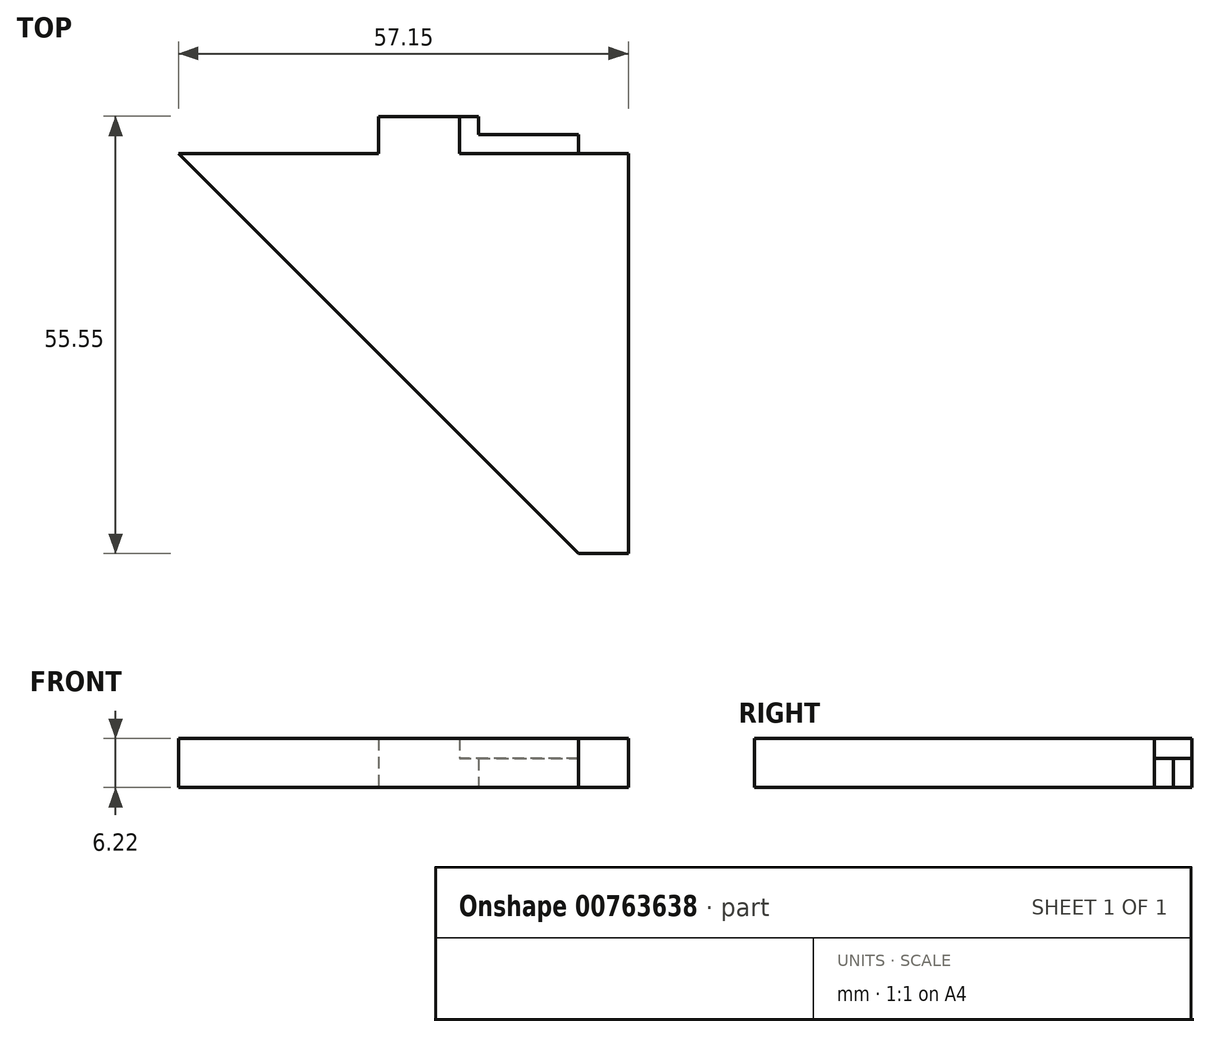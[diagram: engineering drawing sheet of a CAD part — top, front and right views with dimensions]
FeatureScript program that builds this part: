
annotation { "Feature Type Name" : "Feature", "Feature Type Description" : "" }
export const myFeature = defineFeature(function(context is Context, id is Id, definition is map)
    precondition{}
    {
        {
            var Q0;
            Q0=qCreatedBy(makeId("Top.planeOp"),FACE);
            var sketch = newSketch(context, id + "F0", { "sketchPlane" : qUnion([Q0])});
            skLineSegment(sketch, "E0.bottom", {"start": v(25.4, -25.4) * mm, "end": v(-25.4, -25.4) * mm});
            skLineSegment(sketch, "E0.top", {"start": v(25.4, 25.4) * mm, "end": v(-25.4, 25.4) * mm});
            skLineSegment(sketch, "E0.left", {"start": v(25.4, -25.4) * mm, "end": v(25.4, 25.4) * mm});
            skLineSegment(sketch, "E0.right", {"start": v(-25.4, -25.4) * mm, "end": v(-25.4, 25.4) * mm});
            skPoint(sketch, "E0.middle", {"position": v(0, 0) * mm});
            skLineSegment(sketch, "E1", {"start": v(-25.4, 25.4) * mm, "end": v(25.4, -25.4) * mm});
            skLineSegment(sketch, "E2.bottom", {"start": v(0, 25.4) * mm, "end": v(12.7, 25.4) * mm});
            skLineSegment(sketch, "E2.top", {"start": v(0, 30.15) * mm, "end": v(12.7, 30.15) * mm});
            skLineSegment(sketch, "E2.left", {"start": v(0, 25.4) * mm, "end": v(0, 30.15) * mm});
            skLineSegment(sketch, "E2.right", {"start": v(12.7, 25.4) * mm, "end": v(12.7, 30.15) * mm});
            skLineSegment(sketch, "E3", {"start": v(10.29, 30.15) * mm, "end": v(10.29, 25.4) * mm});
            skLineSegment(sketch, "E4.bottom", {"start": v(12.7, 25.4) * mm, "end": v(25.4, 25.4) * mm});
            skLineSegment(sketch, "E4.top", {"start": v(12.7, 27.81) * mm, "end": v(25.4, 27.81) * mm});
            skLineSegment(sketch, "E4.left", {"start": v(12.7, 25.4) * mm, "end": v(12.7, 27.81) * mm});
            skLineSegment(sketch, "E4.right", {"start": v(25.4, 25.4) * mm, "end": v(25.4, 27.81) * mm});
            skLineSegment(sketch, "E5.bottom", {"start": v(25.4, -25.4) * mm, "end": v(31.75, -25.4) * mm});
            skLineSegment(sketch, "E5.top", {"start": v(25.4, 25.4) * mm, "end": v(31.75, 25.4) * mm});
            skLineSegment(sketch, "E5.right", {"start": v(31.75, -25.4) * mm, "end": v(31.75, 25.4) * mm});
            skSolve(sketch);
        }
        {
            var Q0;
            {var subQ4=sQuery(id+"F0.wireOp",EDGE,"E0.left");Q0=makeQuery(id+"F0.imprint","IMPRINT",FACE,{"disambiguationData":[TD([[makeQuery(id+"F0.imprint","IMPRINT",EDGE,{"derivedFrom":subQ4}),1.0]])]});}
            var Q1;
            {var subQ0=sQuery(id+"F0.wireOp",EDGE,"E2.left");Q1=makeQuery(id+"F0.imprint","IMPRINT",FACE,{"disambiguationData":[TD([[makeQuery(id+"F0.imprint","IMPRINT",EDGE,{"derivedFrom":subQ0}),-1.0]])]});}
            var Q2;
            Q2=makeQuery(id+"F0.imprint","IMPRINT",FACE,{"disambiguationData":[TD([[makeQuery(id+"F0.imprint","IMPRINT",EDGE,{"derivedFrom":sQuery(id+"F0.wireOp",EDGE,"E0.left")}),-1.0]])]});
            extrude(context, id + "F1", {"entities" : qUnion([Q0, Q1, Q2]), "depth" : 6.22 * mm, "offsetDistance" : 25.4 * mm});
        }
        {
            var Q0;
            {var subQ6=sQuery(id+"F0.wireOp",EDGE,"E3");Q0=makeQuery(id+"F0.imprint","IMPRINT",FACE,{"disambiguationData":[TD([[makeQuery(id+"F0.imprint","IMPRINT",EDGE,{"derivedFrom":subQ6}),1.0]])]});}
            var Q1;
            {var subQ4=sQuery(id+"F0.wireOp",EDGE,"E4.top");Q1=makeQuery(id+"F0.imprint","IMPRINT",FACE,{"disambiguationData":[TD([[makeQuery(id+"F0.imprint","IMPRINT",EDGE,{"derivedFrom":subQ4}),-1.0]])]});}
            extrude(context, id + "F2", {"entities" : qUnion([Q0, Q1]), "operationType" : NewBodyOperationType.ADD, "depth" : 3.68 * mm, "offsetDistance" : 25.4 * mm});
        }
    });
